# Revit family: OASIS SHFW-5038
name_source: partatom
category: Plumbing Fixtures
units: mm (PartAtom-declared; Revit-internal decimal feet)

## family parameters
Always vertical = Yes
Cut with Voids When Loaded = No
OmniClass Number = 23.45.05.14.21.11
OmniClass Title = Bath/Shower Units
Part Type = Normal
Room Calculation Point = No
Round Connector Dimension = Use Diameter
Shared = No
Work Plane-Based = No

## types (5) — shared parameters
BIM Model By = www.shive-hattery.com
Cold Water Connector = Cold Water Connection
Color = <By Category>
Default Elevation = 0"
Grab Bar Finish = <By Category>
Hot Water Connector = Hot Water Connection
Manufacturer = OASIS
Sanitary Connector = Sanitary Connection
Seat Finish = <By Category>
Shower Rod = No
Stainless steel = <By Category>
Type Comments = Shower
URL = www.oasisbath.com

## per-type parameters (varying)
| type | Bar_Horz_Back | Bar_Horz_Side | Bar_Vert | Model | Seat_Fold |
| Base Model, 3SF, 3SM, FH, TLVRF packages | No | No | No | SHFW-5038/(Base Model,3SF,3SM,FH,TLVRF) | No |
| BP1 package | Yes | Yes | No | SHFW-5038/BP1 | No |
| BP2 package | Yes | Yes | Yes | SHFW-5038/BP2 | No |
| TL package | Yes | Yes | No | SHFW-5038/TL | Yes |
| TLV package | Yes | Yes | Yes | SHFW-5038/TLV | Yes |

## geometry (parser evidence)
native form markers: Sweep x8
no freeform markers — native parametric forms only
